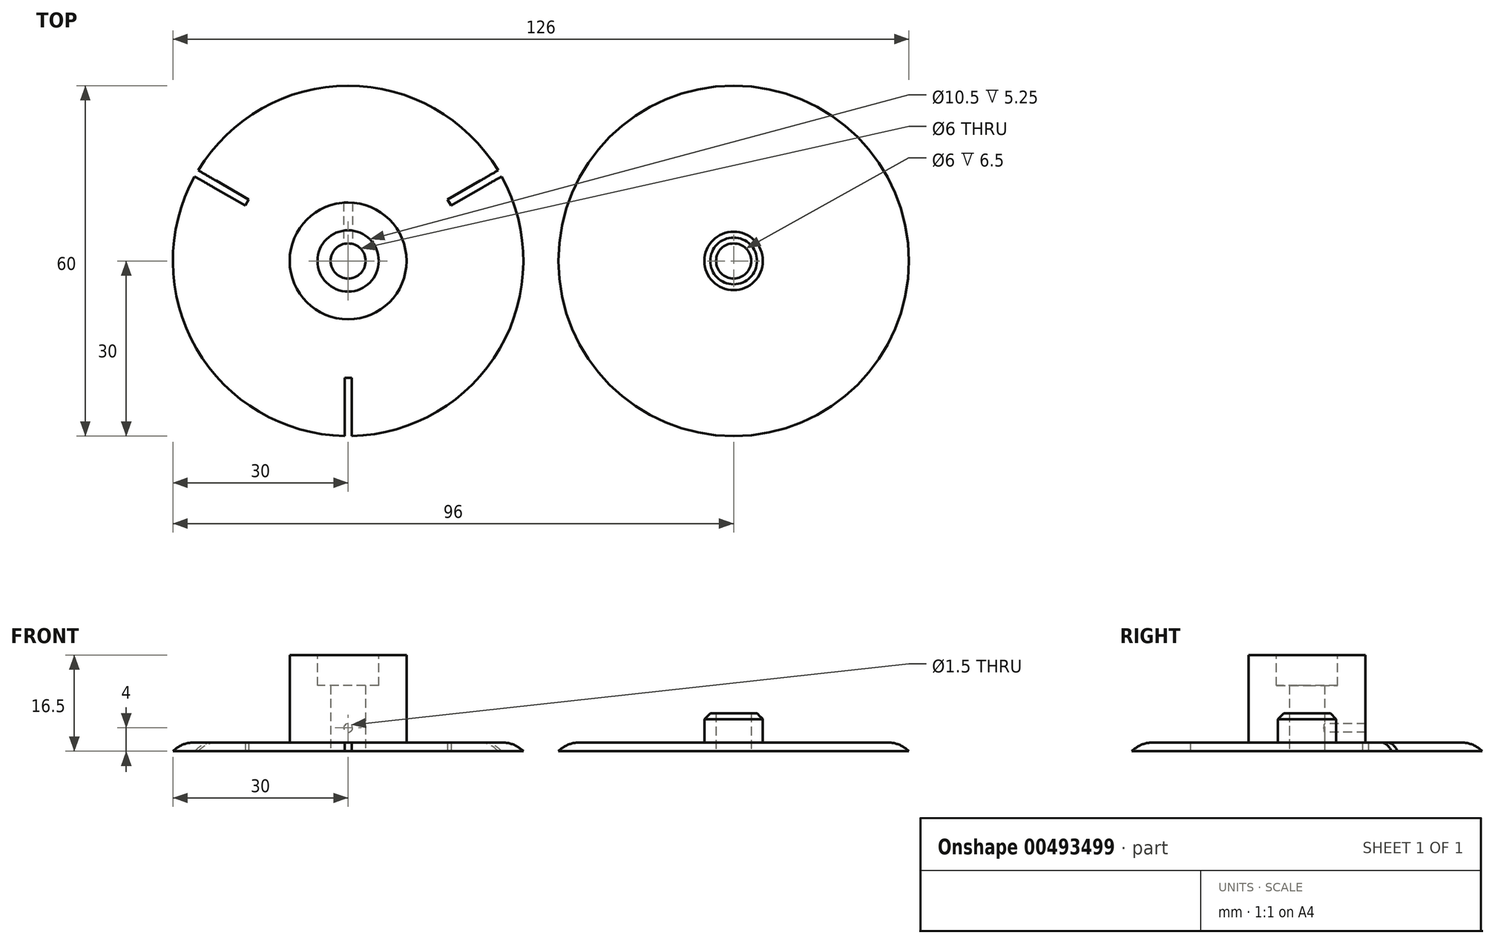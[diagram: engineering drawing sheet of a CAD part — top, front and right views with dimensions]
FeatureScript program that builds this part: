
annotation { "Feature Type Name" : "Feature", "Feature Type Description" : "" }
export const myFeature = defineFeature(function(context is Context, id is Id, definition is map)
    precondition{}
    {
        {
            var Q0;
            Q0=qCreatedBy(makeId("Top.planeOp"),FACE);
            var sketch = newSketch(context, id + "F0", { "sketchPlane" : qUnion([Q0])});
            skCircle(sketch, "E0", {"center": v(-33, 0) * mm, "radius": 30 * mm});
            skCircle(sketch, "E1", {"center": v(33, 0) * mm, "radius": 30 * mm});
            skSolve(sketch);
        }
        {
            var Q0;
            Q0 = qSketchRegion(id + "F0", true);
            extrude(context, id + "F1", {"entities" : qUnion([Q0]), "depth" : 1.5 * mm});
        }
        {
            var Q0;
            Q0=makeQuery(id+"F1.opExtrude","CAP_EDGE",EDGE,{"disambiguationData":[OSD([sQuery(id+"F0.wireOp",EDGE,"E0")])],"isStart":false});
            var Q1;
            Q1=makeQuery(id+"F1.opExtrude","CAP_EDGE",EDGE,{"disambiguationData":[OSD([sQuery(id+"F0.wireOp",EDGE,"E1")])],"isStart":false});
            fillet(context, id + "F2", {"entities" : qUnion([Q0, Q1]), "radius" : 5 * mm, "tangentPropagation" : true, "allowEdgeOverflow" : false});
        }
        {
            var Q0;
            Q0=makeQuery(id+"F1.opExtrude","CAP_FACE",FACE,{"disambiguationData":[OSD([sQuery(id+"F0.wireOp",EDGE,"E0")])],"isStart":false});
            var sketch = newSketch(context, id + "F3", { "sketchPlane" : qUnion([Q0])});
            skCircle(sketch, "E2", {"center": v(-33, 0) * mm, "radius": 10 * mm});
            skSolve(sketch);
        }
        {
            var Q0;
            Q0=makeQuery(id+"F3.imprint","IMPRINT",FACE,{"disambiguationData":[TD([[makeQuery(id+"F3.imprint","IMPRINT",EDGE,{"derivedFrom":sQuery(id+"F3.wireOp",EDGE,"E2")}),1.0]])]});
            extrude(context, id + "F4", {"entities" : qUnion([Q0]), "operationType" : NewBodyOperationType.ADD, "depth" : 15 * mm});
        }
        {
            var Q0;
            Q0=makeQuery(id+"F1.opExtrude","CAP_FACE",FACE,{"disambiguationData":[OSD([sQuery(id+"F0.wireOp",EDGE,"E1")])],"isStart":false});
            var sketch = newSketch(context, id + "F5", { "sketchPlane" : qUnion([Q0])});
            skCircle(sketch, "E3", {"center": v(33, 0) * mm, "radius": 5 * mm});
            skSolve(sketch);
        }
        {
            var Q0;
            Q0=makeQuery(id+"F5.imprint","IMPRINT",FACE,{"disambiguationData":[TD([[makeQuery(id+"F5.imprint","IMPRINT",EDGE,{"derivedFrom":sQuery(id+"F5.wireOp",EDGE,"E3")}),1.0]])]});
            extrude(context, id + "F6", {"entities" : qUnion([Q0]), "operationType" : NewBodyOperationType.ADD, "depth" : 5 * mm});
        }
        {
            var Q0;
            Q0=makeQuery(id+"F4.opExtrude","CAP_FACE",FACE,{"disambiguationData":[OSD([sQuery(id+"F3.wireOp",EDGE,"E2")])],"isStart":false});
            var sketch = newSketch(context, id + "F7", { "sketchPlane" : qUnion([Q0])});
            skCircle(sketch, "E4", {"center": v(-33, 0) * mm, "radius": 5.25 * mm});
            skSolve(sketch);
        }
        {
            var Q0;
            Q0=makeQuery(id+"F7.imprint","IMPRINT",FACE,{"disambiguationData":[TD([[makeQuery(id+"F7.imprint","IMPRINT",EDGE,{"derivedFrom":sQuery(id+"F7.wireOp",EDGE,"E4")}),1.0]])]});
            extrude(context, id + "F8", {"entities" : qUnion([Q0]), "operationType" : NewBodyOperationType.REMOVE, "oppositeDirection" : true, "depth" : 5.25 * mm});
        }
        {
            var Q0;
            Q0=makeQuery(id+"F1.opExtrude","CAP_FACE",FACE,{"disambiguationData":[OSD([sQuery(id+"F0.wireOp",EDGE,"E1")])],"isStart":true});
            var sketch = newSketch(context, id + "F9", { "sketchPlane" : qUnion([Q0])});
            skCircle(sketch, "E5", {"center": v(33, 0) * mm, "radius": 3 * mm});
            skSolve(sketch);
        }
        {
            var Q0;
            Q0=makeQuery(id+"F1.opExtrude","CAP_FACE",FACE,{"disambiguationData":[OSD([sQuery(id+"F0.wireOp",EDGE,"E0")])],"isStart":true});
            var sketch = newSketch(context, id + "F10", { "sketchPlane" : qUnion([Q0])});
            skCircle(sketch, "E6", {"center": v(-33, 0) * mm, "radius": 3 * mm});
            skSolve(sketch);
        }
        {
            var Q0;
            Q0 = qSketchRegion(id + "F9", true);
            extrude(context, id + "F11", {"entities" : qUnion([Q0]), "operationType" : NewBodyOperationType.REMOVE, "oppositeDirection" : true, "depth" : 25 * mm});
        }
        {
            var Q0;
            Q0=makeQuery(id+"F10.imprint","IMPRINT",FACE,{"disambiguationData":[TD([[makeQuery(id+"F10.imprint","IMPRINT",EDGE,{"derivedFrom":sQuery(id+"F10.wireOp",EDGE,"E6")}),1.0]])]});
            extrude(context, id + "F12", {"entities" : qUnion([Q0]), "operationType" : NewBodyOperationType.REMOVE, "oppositeDirection" : true, "depth" : 25 * mm});
        }
        {
            var Q0;
            Q0=qCreatedBy(makeId("Front.planeOp"),FACE);
            var sketch = newSketch(context, id + "F13", { "sketchPlane" : qUnion([Q0])});
            skCircle(sketch, "E7", {"center": v(-33, 4) * mm, "radius": 0.75 * mm});
            skSolve(sketch);
        }
        {
            var Q0;
            Q0 = qSketchRegion(id + "F13", true);
            extrude(context, id + "F14", {"entities" : qUnion([Q0]), "operationType" : NewBodyOperationType.REMOVE, "endBound" : BoundingType.THROUGH_ALL, "oppositeDirection" : true, "depth" : 25 * mm});
        }
        {
            var Q0;
            Q0=makeQuery(id+"F1.opExtrude","CAP_FACE",FACE,{"disambiguationData":[OSD([sQuery(id+"F0.wireOp",EDGE,"E0")])],"isStart":true});
            var sketch = newSketch(context, id + "F15", { "sketchPlane" : qUnion([Q0])});
            skLineSegment(sketch, "E8", {"start": v(-33, 0) * mm, "end": v(-33, 30) * mm, "construction": true});
            skLineSegment(sketch, "E9", {"start": v(-33, 0) * mm, "end": v(-33, -30) * mm, "construction": true});
            skLineSegment(sketch, "E10", {"start": v(-63, 0) * mm, "end": v(-3, 0) * mm, "construction": true});
            skLineSegment(sketch, "E11.bottom", {"start": v(-32.4, 20) * mm, "end": v(-33.6, 20) * mm});
            skLineSegment(sketch, "E11.top", {"start": v(-32.4, 40) * mm, "end": v(-33.6, 40) * mm});
            skLineSegment(sketch, "E11.left", {"start": v(-32.4, 20) * mm, "end": v(-32.4, 40) * mm});
            skLineSegment(sketch, "E11.right", {"start": v(-33.6, 20) * mm, "end": v(-33.6, 40) * mm});
            skPoint(sketch, "E11.middle", {"position": v(-33, 30) * mm});
            skLineSegment(sketch, "E12.1.0", {"start": v(-50.02, -10.52) * mm, "end": v(-67.34, -20.52) * mm});
            skLineSegment(sketch, "E12.1.1", {"start": v(-50.62, -9.48) * mm, "end": v(-67.94, -19.48) * mm});
            skLineSegment(sketch, "E12.1.2", {"start": v(-50.62, -9.48) * mm, "end": v(-50.02, -10.52) * mm});
            skLineSegment(sketch, "E12.1.3", {"start": v(-67.94, -19.48) * mm, "end": v(-67.34, -20.52) * mm});
            skLineSegment(sketch, "E12.2.0", {"start": v(-15.38, -9.48) * mm, "end": v(1.94, -19.48) * mm});
            skLineSegment(sketch, "E12.2.1", {"start": v(-15.98, -10.52) * mm, "end": v(1.34, -20.52) * mm});
            skLineSegment(sketch, "E12.2.2", {"start": v(-15.98, -10.52) * mm, "end": v(-15.38, -9.48) * mm});
            skLineSegment(sketch, "E12.2.3", {"start": v(1.34, -20.52) * mm, "end": v(1.94, -19.48) * mm});
            skPoint(sketch, "E12.center", {"position": v(-33, 0) * mm});
            skSolve(sketch);
        }
        {
            var Q0;
            Q0 = qSketchRegion(id + "F15", true);
            extrude(context, id + "F16", {"entities" : qUnion([Q0]), "operationType" : NewBodyOperationType.REMOVE, "oppositeDirection" : true, "depth" : 25 * mm});
        }
        {
            var Q0;
            Q0=makeQuery(id+"F8.boolean.opBoolean","COPY",EDGE,{"derivedFrom":makeQuery(id+"F8.opExtrude","CAP_EDGE",EDGE,{"disambiguationData":[OSD([sQuery(id+"F7.wireOp",EDGE,"E4")])],"isStart":true})});
            var Q1;
            Q1=makeQuery(id+"F6.opExtrude","CAP_EDGE",EDGE,{"disambiguationData":[OSD([sQuery(id+"F5.wireOp",EDGE,"E3")])],"isStart":false});
            chamfer(context, id + "F17", {"entities" : qUnion([Q0, Q1]), "width" : 1 * mm, "tangentPropagation" : true});
        }
    });
